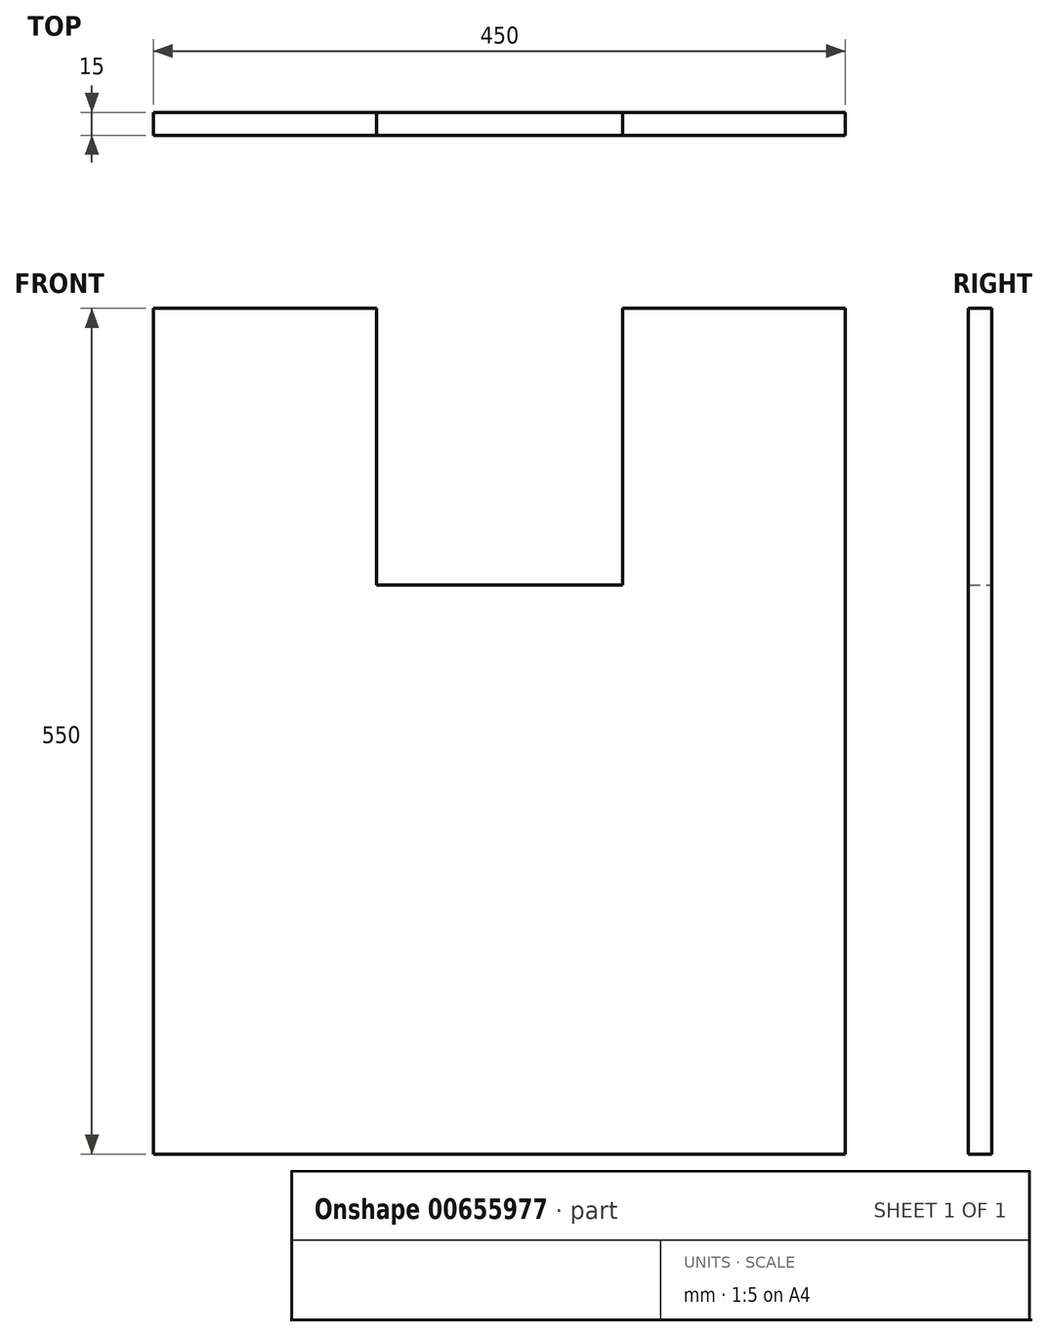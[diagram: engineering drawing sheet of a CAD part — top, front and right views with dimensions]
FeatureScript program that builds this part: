
annotation { "Feature Type Name" : "Feature", "Feature Type Description" : "" }
export const myFeature = defineFeature(function(context is Context, id is Id, definition is map)
    precondition{}
    {
        {
            var Q0;
            Q0=qCreatedBy(makeId("Front.planeOp"),FACE);
            var sketch = newSketch(context, id + "F0", { "sketchPlane" : qUnion([Q0])});
            skLineSegment(sketch, "E0.bottom", {"start": v(0, 0) * mm, "end": v(450, 0) * mm});
            skLineSegment(sketch, "E0.top", {"start": v(0, 550) * mm, "end": v(450, 550) * mm});
            skLineSegment(sketch, "E0.left", {"start": v(0, 0) * mm, "end": v(0, 550) * mm});
            skLineSegment(sketch, "E0.right", {"start": v(450, 0) * mm, "end": v(450, 550) * mm});
            skLineSegment(sketch, "E1", {"start": v(145, 550) * mm, "end": v(145, 370) * mm});
            skLineSegment(sketch, "E2", {"start": v(145, 370) * mm, "end": v(305, 370) * mm});
            skLineSegment(sketch, "E3", {"start": v(305, 370) * mm, "end": v(305, 550) * mm});
            skSolve(sketch);
        }
        {
            var Q0;
            Q0=makeQuery(id+"F0.imprint","IMPRINT",FACE,{"disambiguationData":[TD([[makeQuery(id+"F0.imprint","IMPRINT",EDGE,{"derivedFrom":sQuery(id+"F0.wireOp",EDGE,"E0.bottom")}),1.0]])]});
            extrude(context, id + "F1", {"entities" : qUnion([Q0]), "depth" : 15 * mm, "offsetDistance" : 25.4 * mm});
        }
    });
